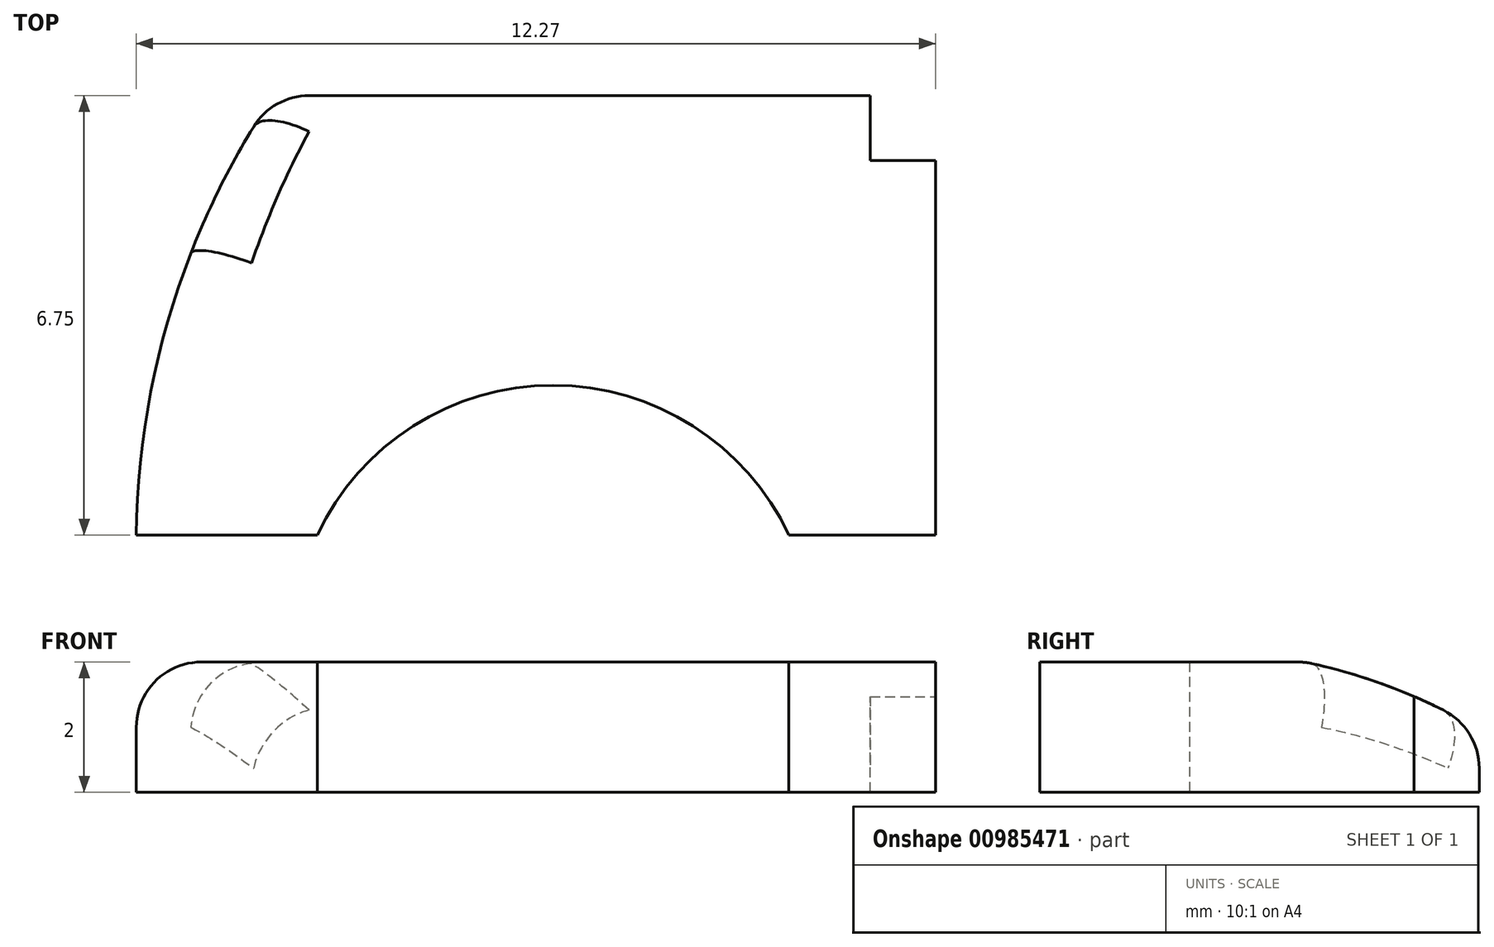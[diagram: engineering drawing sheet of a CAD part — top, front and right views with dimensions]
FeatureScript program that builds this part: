
annotation { "Feature Type Name" : "Feature", "Feature Type Description" : "" }
export const myFeature = defineFeature(function(context is Context, id is Id, definition is map)
    precondition{}
    {
        {
            var Q0;
            Q0=qCreatedBy(makeId("Top.planeOp"),FACE);
            var sketch = newSketch(context, id + "F0", { "sketchPlane" : qUnion([Q0])});
            skArc(sketch, "E0", {"start": v(0, 0) * mm, "mid": v(-3.62, 2.3) * mm, "end": v(-7.24, 0) * mm});
            skLineSegment(sketch, "E1", {"start": v(-7.24, 0) * mm, "end": v(-10.02, 0) * mm});
            skArc(sketch, "E2", {"start": v(-7.91, 6.75) * mm, "mid": v(-9.46, 3.53) * mm, "end": v(-10.02, 0) * mm});
            skLineSegment(sketch, "E3", {"start": v(-7.91, 6.75) * mm, "end": v(2.25, 6.75) * mm});
            skLineSegment(sketch, "E4", {"start": v(2.25, 6.75) * mm, "end": v(2.25, 0) * mm});
            skLineSegment(sketch, "E5", {"start": v(2.25, 0) * mm, "end": v(0, 0) * mm});
            skSolve(sketch);
        }
        {
            var Q0;
            Q0=qSketchRegion(id+"F0",true);
            extrude(context, id + "F1", {"entities" : qUnion([Q0]), "depth" : 2 * mm});
        }
        {
            var Q0;
            Q0=makeQuery(id+"F1.opExtrude","SWEPT_FACE",FACE,{"disambiguationData":[OSD([sQuery(id+"F0.wireOp",EDGE,"E4")])]});
            var sketch = newSketch(context, id + "F2", { "sketchPlane" : qUnion([Q0])});
            skLineSegment(sketch, "E6", {"start": v(1.3, 1.98) * mm, "end": v(1.3, 1.98) * mm});
            skArc(sketch, "E7", {"start": v(7.25, 0.64) * mm, "mid": v(5.78, 1.46) * mm, "end": v(4.18, 1.98) * mm});
            skPoint(sketch, "E8.visualSharp", {"position": v(8.37, -0.29) * mm});
            skPoint(sketch, "E9.visualSharp", {"position": v(12.01, -0.29) * mm});
            skPoint(sketch, "E10.visualSharp", {"position": v(4.07, 2) * mm});
            skArc(sketch, "E10.filletArc", {"start": v(4.18, 1.98) * mm, "mid": v(4.07, 2) * mm, "end": v(3.96, 2) * mm});
            skLineSegment(sketch, "E11", {"start": v(5.8, 3.91) * mm, "end": v(3.96, 2) * mm});
            skLineSegment(sketch, "E12", {"start": v(5.8, 3.91) * mm, "end": v(8.9, 2.87) * mm});
            skLineSegment(sketch, "E13", {"start": v(8.9, 2.87) * mm, "end": v(7.25, 0.64) * mm});
            skSolve(sketch);
        }
        {
            var Q0;
            Q0=qSketchRegion(id+"F2",true);
            extrude(context, id + "F3", {"entities" : qUnion([Q0]), "operationType" : NewBodyOperationType.REMOVE, "endBound" : BoundingType.THROUGH_ALL, "oppositeDirection" : true, "depth" : 25 * mm});
        }
        {
            var Q0;
            Q0=makeQuery(id+"F1.opExtrude","SWEPT_EDGE",EDGE,{"disambiguationData":[OSD([sQuery(id+"F0.wireOp",EDGE,"E2"),sQuery(id+"F0.wireOp",EDGE,"E3")])]});
            var Q1;
            Q1=makeQuery(id+"F3.boolean.opBoolean","INTERSECT",EDGE,{"derivedFrom":[makeQuery(id+"F1.opExtrude","SWEPT_FACE",FACE,{"disambiguationData":[OSD([sQuery(id+"F0.wireOp",EDGE,"E2")])]}),makeQuery(id+"F3.opExtrude","SWEPT_FACE",FACE,{"disambiguationData":[OSD([sQuery(id+"F2.wireOp",EDGE,"E7")])]})]});
            fillet(context, id + "F4", {"entities" : qUnion([Q0, Q1]), "radius" : 1 * mm, "tangentPropagation" : true, "allowEdgeOverflow" : false});
        }
        {
            var Q0;
            {var subQ0=sQuery(id+"F0.wireOp",EDGE,"E2");Q0=makeQuery(id+"F4.opFillet","BLEND_EDGE",EDGE,{"blendedFrom":[makeQuery(id+"F1.opExtrude","SWEPT_EDGE",EDGE,{"disambiguationData":[OSD([subQ0,sQuery(id+"F0.wireOp",EDGE,"E3")])]}),makeQuery(id+"F3.boolean.opBoolean","INTERSECT",EDGE,{"derivedFrom":[makeQuery(id+"F1.opExtrude","SWEPT_FACE",FACE,{"disambiguationData":[OSD([subQ0])]}),makeQuery(id+"F3.opExtrude","SWEPT_FACE",FACE,{"disambiguationData":[OSD([sQuery(id+"F2.wireOp",EDGE,"E7")])]})]})],"blendedInto":[]});}
            fillet(context, id + "F5", {"entities" : qUnion([Q0]), "radius" : 1 * mm, "tangentPropagation" : true, "allowEdgeOverflow" : false});
        }
        {
            var Q0;
            Q0=makeQuery(id+"F1.opExtrude","SWEPT_FACE",FACE,{"disambiguationData":[OSD([sQuery(id+"F0.wireOp",EDGE,"E3")])]});
            var sketch = newSketch(context, id + "F6", { "sketchPlane" : qUnion([Q0])});
            skLineSegment(sketch, "E14.bottom", {"start": v(-2.25, 0) * mm, "end": v(-1.25, 0) * mm});
            skLineSegment(sketch, "E14.top", {"start": v(-2.25, 1.98) * mm, "end": v(-1.25, 1.98) * mm});
            skLineSegment(sketch, "E14.left", {"start": v(-2.25, 0) * mm, "end": v(-2.25, 1.98) * mm});
            skLineSegment(sketch, "E14.right", {"start": v(-1.25, 0) * mm, "end": v(-1.25, 1.98) * mm});
            skSolve(sketch);
        }
        {
            var Q0;
            Q0=qSketchRegion(id+"F6",true);
            extrude(context, id + "F7", {"entities" : qUnion([Q0]), "operationType" : NewBodyOperationType.REMOVE, "oppositeDirection" : true, "depth" : 1 * mm});
        }
    });
